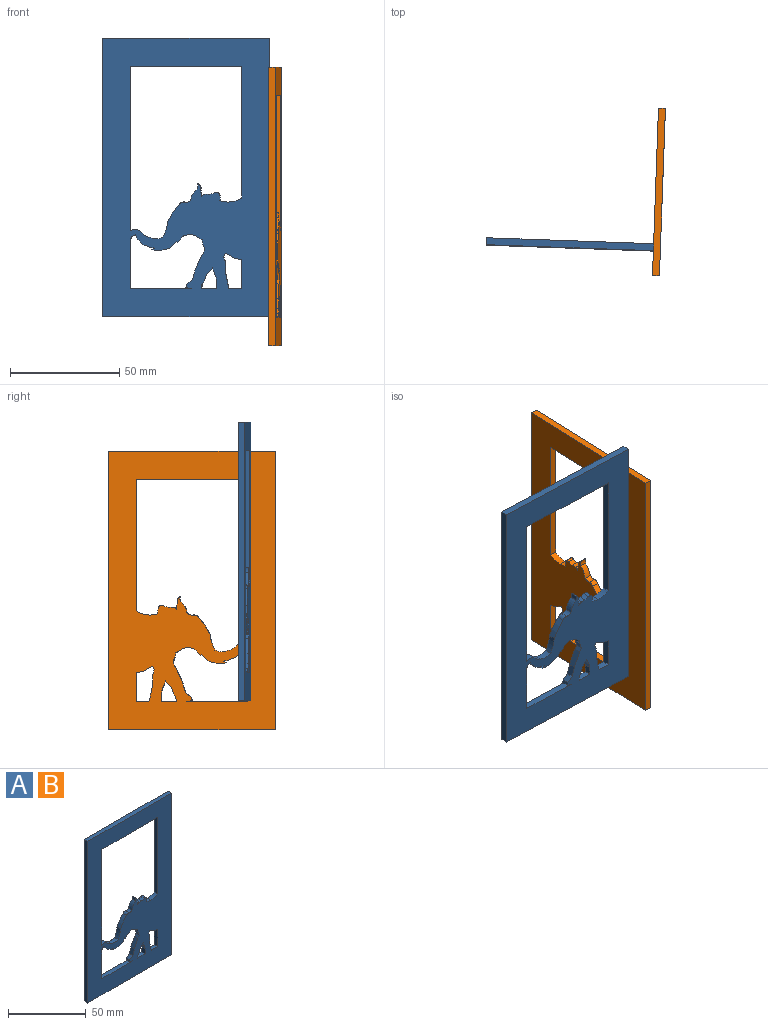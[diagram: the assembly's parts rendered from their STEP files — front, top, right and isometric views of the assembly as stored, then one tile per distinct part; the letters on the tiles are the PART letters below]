
ASSEMBLY  parts=2 mates=1
PART A: 69 faces, bbox 76.2x3.2x127 mm
  f0: plane 3.78x3.18mm, normal (-1,0,0), area 12mm2, adj f1,f66,f67,f68
  f1: plane 6.84x3.18mm, normal (0,0,1), area 21.7mm2, adj f0,f2,f67,f68
  f2: plane 3.18x1.9mm, normal (1,0,-0.07), area 6mm2, adj f1,f3,f67,f68
  f3: plane 3.18x2.23mm, normal (0.87,0,-0.49), area 8.1mm2, adj f2,f4,f67,f68
  f4: plane 3.18x2.3mm, normal (0.95,0,-0.32), area 7.7mm2, adj f3,f5,f67,f68
  f5: plane 3.18x3.07mm, normal (0.75,0,-0.66), area 13mm2, adj f4,f6,f67,f68
  f6: plane 3.49x3.18mm, normal (-0.93,0,-0.37), area 11.9mm2, adj f5,f66,f67,f68
  f7: cylinder r=23.13mm len=3.18mm, axis (0,1,0), area 9mm2, adj f8,f62,f67,f68
  f8: plane 13.27x3.18mm, normal (-1,0,0), area 42.1mm2, adj f7,f9,f67,f68
  f9: plane 5.77x3.18mm, normal (0,0,1), area 18.3mm2, adj f8,f10,f67,f68
  f10: plane 3.62x3.18mm, normal (0.97,0,0.24), area 11.8mm2, adj f9,f11,f67,f68
  f11: plane 4.32x3.18mm, normal (0.98,0,0.18), area 14mm2, adj f10,f12,f67,f68
  f12: plane 4.4x3.18mm, normal (1,0,0), area 14mm2, adj f11,f13,f67,f68
  f13: plane 3.18x2.24mm, normal (0.94,0,0.35), area 7.6mm2, adj f12,f14,f67,f68
  f14: plane 3.18x1.58mm, normal (0.88,0,-0.47), area 5.7mm2, adj f13,f62,f67,f68
  f15: plane 76.21x3.18mm, normal (0,0,1), area 242mm2, adj f16,f63,f67,f68
  f16: plane 127x3.18mm, normal (-1,0,0), area 403.2mm2, adj f15,f17,f67,f68
  f17: plane 76.21x3.18mm, normal (0,0,-1), area 242mm2, adj f16,f63,f67,f68
  f18: cylinder r=0.51mm len=3.18mm, axis (0,1,0), area 3mm2, adj f19,f64,f67,f68
  f19: cylinder r=3.52mm len=3.18mm, axis (0,1,0), area 6.9mm2, adj f18,f20,f67,f68
  f20: cylinder r=14.26mm len=3.85mm, axis (0,1,0), area 15.2mm2, adj f19,f21,f67,f68
  f21: cylinder r=14.73mm len=5.86mm, axis (0,1,0), area 20mm2, adj f20,f22,f67,f68
  f22: plane 3.18x1.4mm, normal (-0.41,0,0.91), area 4.9mm2, adj f21,f23,f67,f68
  f23: cylinder r=12.26mm len=9.3mm, axis (0,1,0), area 30.6mm2, adj f22,f24,f67,f68
  f24: plane 3.18x2.5mm, normal (0.74,0,-0.67), area 10.7mm2, adj f23,f25,f67,f68
  f25: plane 3.18x0.46mm, normal (-0.67,0,-0.74), area 1.9mm2, adj f24,f26,f67,f68
  f26: plane 3.18x1.4mm, normal (0.74,0,-0.67), area 6mm2, adj f25,f27,f67,f68
  f27: plane 3.18x1.26mm, normal (0.71,0,-0.71), area 5.6mm2, adj f26,f28,f67,f68
  f28: plane 3.18x2.86mm, normal (0.32,0,-0.95), area 9.6mm2, adj f27,f29,f67,f68
  f29: plane 3.18x2.86mm, normal (-0.24,0,-0.97), area 9.3mm2, adj f28,f30,f67,f68
  f30: plane 3.18x3.07mm, normal (-0.54,0,-0.84), area 11.6mm2, adj f29,f31,f67,f68
  f31: plane 3.18x1.26mm, normal (-1,0,0), area 4mm2, adj f30,f32,f67,f68
  f32: plane 3.18x1.25mm, normal (-0.86,0,-0.51), area 4.6mm2, adj f31,f33,f67,f68
  f33: plane 3.18x2.44mm, normal (-0.99,0,-0.17), area 7.9mm2, adj f32,f34,f67,f68
  f34: plane 3.18x1.74mm, normal (-0.84,0,0.54), area 6.6mm2, adj f33,f35,f67,f68
  f35: plane 6.98x3.21mm, normal (-0.91,0,0.42), area 24.4mm2, adj f34,f36,f67,f68
  f36: plane 4.47x3.18mm, normal (-0.96,0,0.27), area 14.7mm2, adj f35,f37,f67,f68
  f37: plane 3.18x2.72mm, normal (-0.62,0,0.78), area 11mm2, adj f36,f38,f67,f68
  f38: plane 3.18x1.38mm, normal (-0.98,0,0.22), area 4.5mm2, adj f37,f39,f67,f68
  f39: plane 3.18x2.75mm, normal (-0.22,0,-0.98), area 8.9mm2, adj f38,f40,f67,f68
  f40: plane 28.07x3.18mm, normal (0,0,1), area 89.1mm2, adj f39,f64,f67,f68
  f41: cylinder r=4.44mm len=4.05mm, axis (0,1,0), area 13.5mm2, adj f42,f65,f67,f68
  f42: cylinder r=5.23mm len=3.18mm, axis (0,1,0), area 1.6mm2, adj f41,f43,f67,f68
  f43: plane 75.12x3.18mm, normal (1,0,0), area 238.5mm2, adj f42,f44,f67,f68
  f44: plane 50.81x3.18mm, normal (0,0,-1), area 161.3mm2, adj f43,f45,f67,f68
  f45: plane 60.16x3.18mm, normal (-1,0,0), area 191mm2, adj f44,f46,f67,f68
  f46: cylinder r=10.8mm len=6.47mm, axis (0,1,0), area 21.7mm2, adj f45,f47,f67,f68
  f47: cylinder r=94.94mm len=3.44mm, axis (0,1,0), area 11mm2, adj f46,f48,f67,f68
  f48: cylinder r=6.82mm len=3.18mm, axis (0,1,0), area 9.9mm2, adj f47,f49,f67,f68
  f49: cylinder r=1.53mm len=3.18mm, axis (0,1,0), area 7.6mm2, adj f48,f50,f67,f68
  f50: cylinder r=10.24mm len=3.18mm, axis (0,1,0), area 7.7mm2, adj f49,f51,f67,f68
  f51: cylinder r=14.62mm len=3.18mm, axis (0,1,0), area 7.1mm2, adj f50,f52,f67,f68
  f52: cylinder r=1.91mm len=3.18mm, axis (0,1,0), area 6.3mm2, adj f51,f53,f67,f68
  f53: cylinder r=49.77mm len=3.18mm, axis (0,1,0), area 9.7mm2, adj f52,f54,f67,f68
  f54: cylinder r=2.37mm len=3.18mm, axis (0,1,0), area 10.6mm2, adj f53,f55,f67,f68
  f55: cylinder r=5.13mm len=3.18mm, axis (0,1,0), area 7.3mm2, adj f54,f56,f67,f68
  f56: cylinder r=9.13mm len=5.25mm, axis (0,1,0), area 19.7mm2, adj f55,f57,f67,f68
  f57: cylinder r=2.92mm len=3.18mm, axis (0,1,0), area 9.5mm2, adj f56,f58,f67,f68
  f58: cylinder r=2.43mm len=3.18mm, axis (0,1,0), area 8.6mm2, adj f57,f59,f67,f68
  f59: cylinder r=29.94mm len=7.69mm, axis (0,1,0), area 29.9mm2, adj f58,f60,f67,f68
  f60: cylinder r=18.34mm len=7.3mm, axis (0,1,0), area 24.4mm2, adj f59,f61,f67,f68
  f61: cylinder r=7.38mm len=6.47mm, axis (0,1,0), area 21.3mm2, adj f60,f65,f67,f68
  f62: plane 4.64x3.18mm, normal (-0.47,0,-0.88), area 16.7mm2, adj f7,f14,f67,f68
  f63: plane 127x3.18mm, normal (1,0,0), area 403.2mm2, adj f15,f17,f67,f68
  f64: plane 22.72x3.18mm, normal (1,0,0), area 72.1mm2, adj f18,f40,f67,f68
  f65: cylinder r=8.76mm len=3.9mm, axis (0,1,0), area 15.2mm2, adj f41,f61,f67,f68
  f66: plane 3.18x2.23mm, normal (-0.97,0,-0.24), area 7.3mm2, adj f0,f6,f67,f68
  f67: plane 127x76.21mm, normal (0,-1,0), area 5522.3mm2, adj f0,f1,f2,f3,f4,f5,f6,f7
  f68: plane 127x76.21mm, normal (0,1,0), area 5522.3mm2, adj f0,f1,f2,f3,f4,f5,f6,f7
PART B: same geometry as A
PLACE A rot(axis=(0,0,-1),2deg) t=(6.55,46.12,-8.14)mm
PLACE B rot(axis=(0,0,1),88deg) t=(8.62,108.16,-21.38)mm
MATE fastened A.f63 <-> B.f68  axis (1,-0.04,0) through (6.34,44.54,59.15)mm
